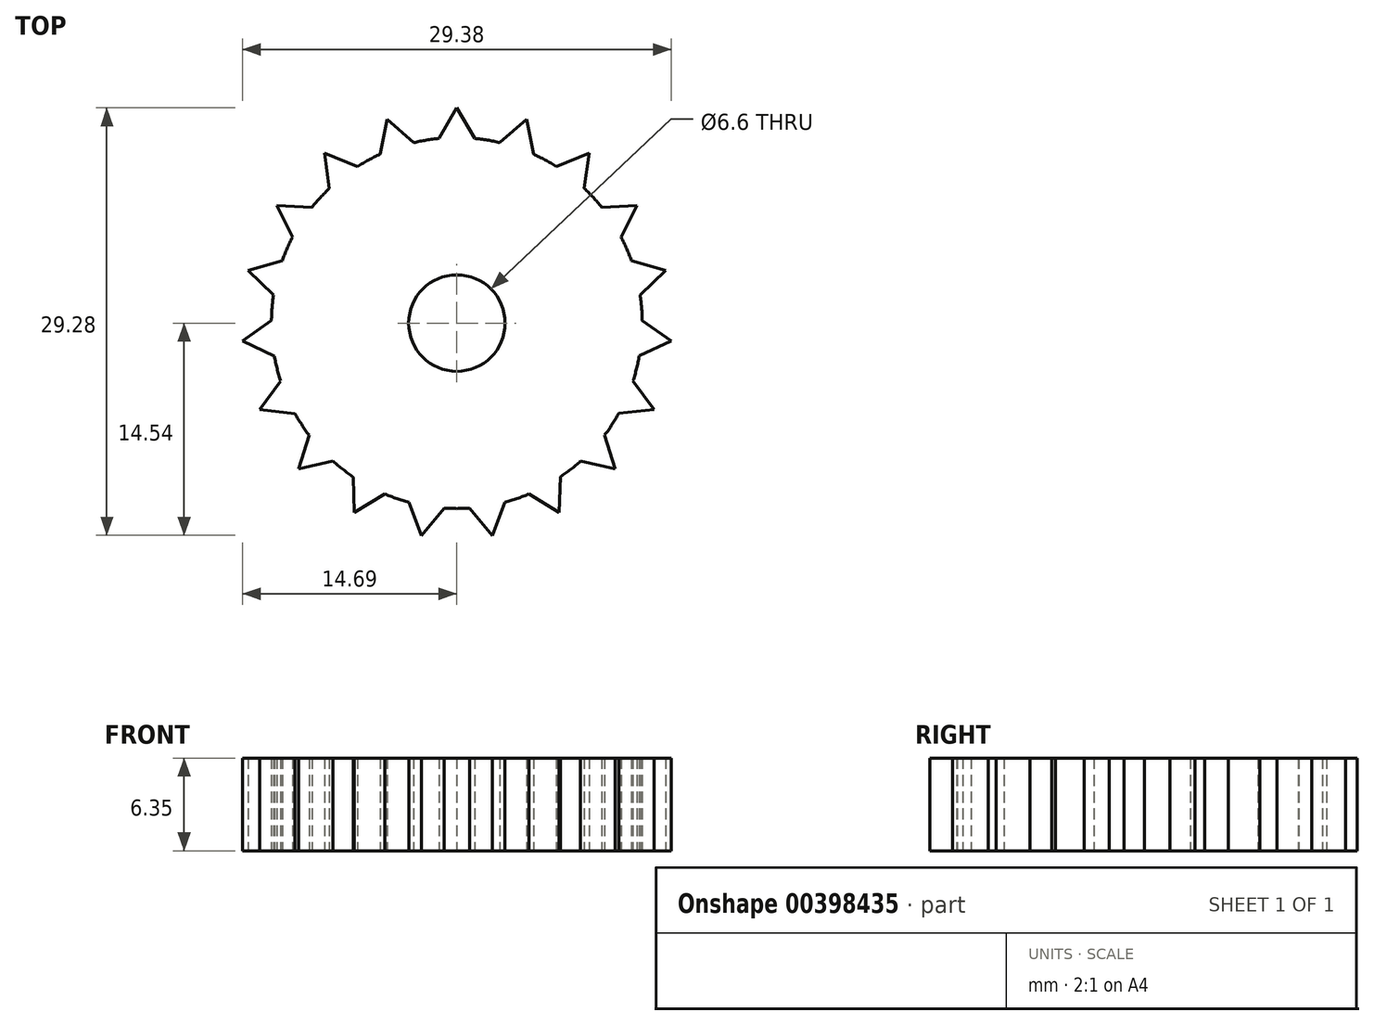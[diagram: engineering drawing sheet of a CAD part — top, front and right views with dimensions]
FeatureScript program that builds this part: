
annotation { "Feature Type Name" : "Feature", "Feature Type Description" : "" }
export const myFeature = defineFeature(function(context is Context, id is Id, definition is map)
    precondition{}
    {
        {
            var Q0;
            Q0=qCreatedBy(makeId("Top.planeOp"),FACE);
            var sketch = newSketch(context, id + "F0", { "sketchPlane" : qUnion([Q0])});
            skCircle(sketch, "E0", {"center": v(0, 0) * mm, "radius": 3.3 * mm});
            skCircle(sketch, "E1", {"center": v(0, 0) * mm, "radius": 12.7 * mm});
            skLineSegment(sketch, "E2", {"start": v(0, 12.7) * mm, "end": v(0, 14.74) * mm});
            skLineSegment(sketch, "E3", {"start": v(0, 14.74) * mm, "end": v(1.21, 12.64) * mm});
            skLineSegment(sketch, "E4", {"start": v(0, 14.74) * mm, "end": v(-1.22, 12.64) * mm});
            skLineSegment(sketch, "E5.1.0", {"start": v(-4.79, 13.94) * mm, "end": v(-2.96, 12.35) * mm});
            skLineSegment(sketch, "E5.1.1", {"start": v(-4.79, 13.94) * mm, "end": v(-5.26, 11.56) * mm});
            skLineSegment(sketch, "E5.2.0", {"start": v(-9.06, 11.63) * mm, "end": v(-6.8, 10.72) * mm});
            skLineSegment(sketch, "E5.2.1", {"start": v(-9.06, 11.63) * mm, "end": v(-8.73, 9.23) * mm});
            skLineSegment(sketch, "E5.3.0", {"start": v(-12.34, 8.06) * mm, "end": v(-9.92, 7.93) * mm});
            skLineSegment(sketch, "E5.3.1", {"start": v(-12.34, 8.06) * mm, "end": v(-11.25, 5.9) * mm});
            skLineSegment(sketch, "E5.4.0", {"start": v(-14.3, 3.62) * mm, "end": v(-11.96, 4.28) * mm});
            skLineSegment(sketch, "E5.4.1", {"start": v(-14.3, 3.62) * mm, "end": v(-12.56, 1.92) * mm});
            skLineSegment(sketch, "E5.5.0", {"start": v(-14.7, -1.22) * mm, "end": v(-12.7, 0.16) * mm});
            skLineSegment(sketch, "E5.5.1", {"start": v(-14.7, -1.22) * mm, "end": v(-12.5, -2.26) * mm});
            skLineSegment(sketch, "E5.6.0", {"start": v(-13.5, -5.92) * mm, "end": v(-12.07, -3.97) * mm});
            skLineSegment(sketch, "E5.6.1", {"start": v(-13.5, -5.92) * mm, "end": v(-11.09, -6.2) * mm});
            skLineSegment(sketch, "E5.7.0", {"start": v(-10.85, -9.99) * mm, "end": v(-10.12, -7.67) * mm});
            skLineSegment(sketch, "E5.7.1", {"start": v(-10.85, -9.99) * mm, "end": v(-8.47, -9.46) * mm});
            skLineSegment(sketch, "E5.8.0", {"start": v(-7.02, -12.97) * mm, "end": v(-7.08, -10.54) * mm});
            skLineSegment(sketch, "E5.8.1", {"start": v(-7.02, -12.97) * mm, "end": v(-4.94, -11.7) * mm});
            skLineSegment(sketch, "E5.9.0", {"start": v(-2.43, -14.54) * mm, "end": v(-3.28, -12.27) * mm});
            skLineSegment(sketch, "E5.9.1", {"start": v(-2.43, -14.54) * mm, "end": v(-0.88, -12.67) * mm});
            skLineSegment(sketch, "E5.10.0", {"start": v(2.43, -14.54) * mm, "end": v(0.88, -12.67) * mm});
            skLineSegment(sketch, "E5.10.1", {"start": v(2.43, -14.54) * mm, "end": v(3.28, -12.27) * mm});
            skLineSegment(sketch, "E5.11.0", {"start": v(7.02, -12.97) * mm, "end": v(4.95, -11.7) * mm});
            skLineSegment(sketch, "E5.11.1", {"start": v(7.02, -12.97) * mm, "end": v(7.1, -10.54) * mm});
            skLineSegment(sketch, "E5.12.0", {"start": v(10.85, -9.99) * mm, "end": v(8.48, -9.46) * mm});
            skLineSegment(sketch, "E5.12.1", {"start": v(10.85, -9.99) * mm, "end": v(10.13, -7.66) * mm});
            skLineSegment(sketch, "E5.13.0", {"start": v(13.5, -5.92) * mm, "end": v(11.1, -6.19) * mm});
            skLineSegment(sketch, "E5.13.1", {"start": v(13.5, -5.92) * mm, "end": v(12.07, -3.96) * mm});
            skLineSegment(sketch, "E5.14.0", {"start": v(14.7, -1.22) * mm, "end": v(12.5, -2.25) * mm});
            skLineSegment(sketch, "E5.14.1", {"start": v(14.7, -1.22) * mm, "end": v(12.7, 0.17) * mm});
            skLineSegment(sketch, "E5.15.0", {"start": v(14.3, 3.62) * mm, "end": v(12.55, 1.93) * mm});
            skLineSegment(sketch, "E5.15.1", {"start": v(14.3, 3.62) * mm, "end": v(11.96, 4.29) * mm});
            skLineSegment(sketch, "E5.16.0", {"start": v(12.34, 8.06) * mm, "end": v(11.25, 5.9) * mm});
            skLineSegment(sketch, "E5.16.1", {"start": v(12.34, 8.06) * mm, "end": v(9.92, 7.94) * mm});
            skLineSegment(sketch, "E5.17.0", {"start": v(9.06, 11.63) * mm, "end": v(8.72, 9.23) * mm});
            skLineSegment(sketch, "E5.17.1", {"start": v(9.06, 11.63) * mm, "end": v(6.8, 10.73) * mm});
            skLineSegment(sketch, "E5.18.0", {"start": v(4.79, 13.94) * mm, "end": v(5.25, 11.56) * mm});
            skLineSegment(sketch, "E5.18.1", {"start": v(4.79, 13.94) * mm, "end": v(2.95, 12.35) * mm});
            skSolve(sketch);
        }
        {
            var Q0;
            Q0 = qSketchRegion(id + "F0", true);
            extrude(context, id + "F1", {"entities" : qUnion([Q0]), "depth" : 6.35 * mm});
        }
    });
